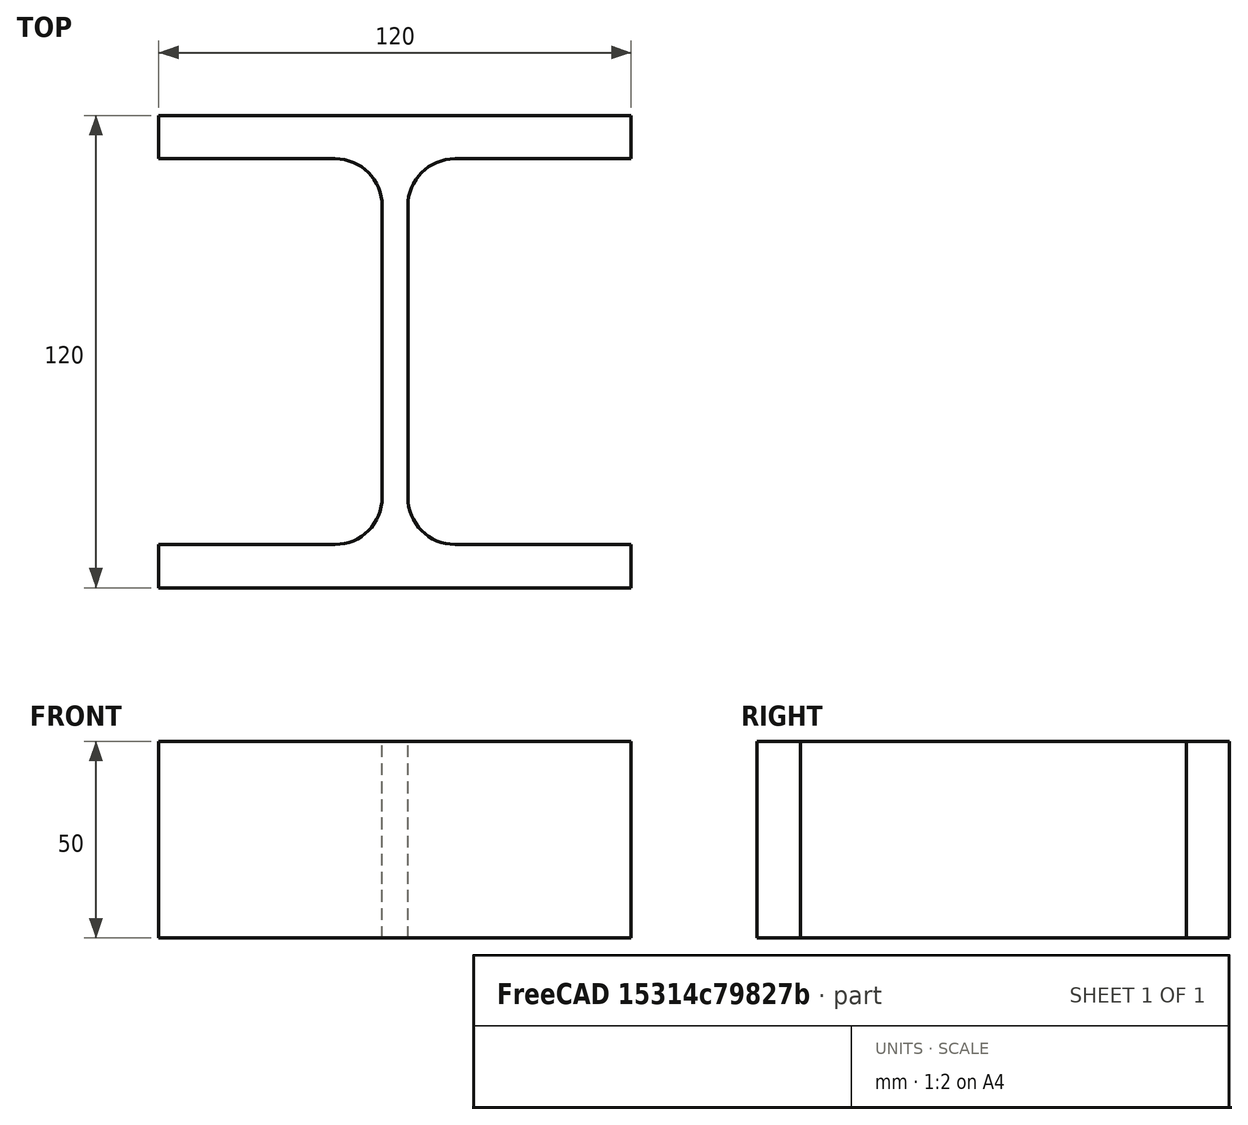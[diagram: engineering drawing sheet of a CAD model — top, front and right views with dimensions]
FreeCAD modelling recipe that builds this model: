
FCSTD DOCUMENT  (FreeCAD 0.15R4671 (Git))
Label: HE-B-Profile 120 DIN1025-2 S235JR
License: All rights reserved
LicenseURL: http://en.wikipedia.org/wiki/All_rights_reserved
objects: Sketcher::SketchObject×1, Part::Extrusion×1
note: 2 computed .brp shape members not serialized (recipe doc carries the construction recipe); baked Part::Feature solids carry a one-line shape summary decoded from their .brp

FEATURE [Sketcher::SketchObject] Sketch
  sketch-geometry (16):
    g0: LineSegment StartX=3.25 StartY=-37 StartZ=0 EndX=3.25 EndY=37 EndZ=0
    g1: LineSegment StartX=15.25 StartY=49 StartZ=0 EndX=60 EndY=49 EndZ=0
    g2: LineSegment StartX=60 StartY=49 StartZ=0 EndX=60 EndY=60 EndZ=0
    g3: LineSegment StartX=60 StartY=60 StartZ=0 EndX=-60 EndY=60 EndZ=0
    g4: LineSegment StartX=-60 StartY=60 StartZ=0 EndX=-60 EndY=49 EndZ=0
    g5: LineSegment StartX=-60 StartY=49 StartZ=0 EndX=-15.25 EndY=49 EndZ=0
    g6: LineSegment StartX=-3.25 StartY=37 StartZ=0 EndX=-3.25 EndY=-37 EndZ=0
    g7: LineSegment StartX=-15.25 StartY=-49 StartZ=0 EndX=-60 EndY=-49 EndZ=0
    g8: LineSegment StartX=-60 StartY=-49 StartZ=0 EndX=-60 EndY=-60 EndZ=0
    g9: LineSegment StartX=-60 StartY=-60 StartZ=0 EndX=60 EndY=-60 EndZ=0
    g10: LineSegment StartX=60 StartY=-60 StartZ=0 EndX=60 EndY=-49 EndZ=0
    g11: LineSegment StartX=60 StartY=-49 StartZ=0 EndX=15.25 EndY=-49 EndZ=0
    g12: ArcOfCircle CenterX=15.25 CenterY=37 CenterZ=0 NormalX=0 NormalY=0 NormalZ=1 Radius=12 StartAngle=1.5708 EndAngle=3.14159
    g13: ArcOfCircle CenterX=15.25 CenterY=-37 CenterZ=0 NormalX=0 NormalY=0 NormalZ=1 Radius=12 StartAngle=3.14159 EndAngle=4.71239
    g14: ArcOfCircle CenterX=-15.25 CenterY=37 CenterZ=0 NormalX=0 NormalY=0 NormalZ=1 Radius=12 StartAngle=0 EndAngle=1.5708
    g15: ArcOfCircle CenterX=-15.25 CenterY=-37 CenterZ=0 NormalX=0 NormalY=0 NormalZ=1 Radius=12 StartAngle=4.71239 EndAngle=6.28319
  constraints (42):
    c: Vertical(g0)
    c: Coincident(g2,g1)
    c: Vertical(g2)
    c: Coincident(g3,g2)
    c: Coincident(g4,g3)
    c: Vertical(g4)
    c: Coincident(g5,g4)
    c: Horizontal(g5)
    c: Vertical(g6)
    c: Horizontal(g7)
    c: Coincident(g8,g7)
    c: Vertical(g8)
    c: Coincident(g9,g8)
    c: Horizontal(g9)
    c: Coincident(g10,g9)
    c: Vertical(g10)
    c: Coincident(g11,g10)
    c: Horizontal(g11)
    c: Tangent(g1,g12) = 1.5708
    c: Tangent(g0,g12) = 1.5708
    c: Tangent(g0,g13) = 1.5708
    c: Tangent(g11,g13) = 1.5708
    c: Tangent(g5,g14) = 1.5708
    c: Tangent(g6,g14) = 1.5708
    c: Tangent(g6,g15) = 1.5708
    c: Tangent(g7,g15) = 1.5708
    c: Equal(g3,g9)
    c: Equal(g2,g4)
    c: Equal(g4,g8)
    c: Equal(g8,g10)
    c: Equal(g12,g14)
    c: Equal(g14,g15)
    c: Equal(g15,g13)
    c: Symmetric(g2,g3,g-2)
    c: Symmetric(g9,g8,g-2)
    c: Symmetric(g0,g6,g-2)
    c: Symmetric(g2,g9,g-1)
    c: DistanceY(g2,g9) = -120
    c: DistanceX(g3) = -120
    c: DistanceX(g0,g6) = -6.5
    c: DistanceY(g2) = 11
    c: Radius(g12) = 12
FEATURE [Part::Extrusion] Extrude  label="HE-B-Profile 120 DIN1025-2 S235JR"
  Base = -> Sketch
  Dir = (0,0,50)
  Solid = true
